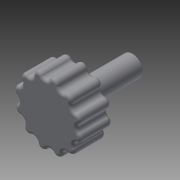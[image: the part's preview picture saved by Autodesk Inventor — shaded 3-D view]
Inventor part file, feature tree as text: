
AUTODESK INVENTOR PART (.ipt)
format: ipt  version: 2015 SP2 (Build 190223200, 223)  size: 412,672 bytes
history: native  units: mm
features: fillet x6, extrude x3, sketch x3, projected_geometry x1
ambient origin geometry x8: Origin, YZ Plane, XZ Plane, XY Plane, X Axis, Y Axis, Z Axis, Center Point
bodies: Body1 (feature_tree)
feature tree (13):
  extrude  "Extrusion2"  Depth=10.0mm
  fillet  "Rundung4"  [1 undecoded]
  fillet  "Rundung5"  Radius=120.0mm
  extrude  "Extrusion3"  Depth=1.0mm
  fillet  "Rundung6"  Radius=4.6mm
  fillet  "Rundung7"  Radius=6.5mm
  extrude  "Extrusion4"  Depth=0.2mm
  fillet  "Rundung8"  Radius=0.2mm
  fillet  "Rundung9"  Radius=3.0mm
  sketch  "Skizze3"  dims[d17=150.0mm d19=360.0deg d21=10.0mm d22=0.0mm d26=30.0mm d27=60.0deg d28=120.0mm d30=360.0deg]
  sketch  "Skizze5"  dims[d32=1.5mm d33=1.0mm d34=4.6mm d35=6.5mm]
  sketch  "Skizze6"  dims[d36=17.0mm d37=0.0mm d38=1.0mm d39=0.2mm d40=3.0mm d41=8.0mm d42=0.0mm d43=0.2mm d44=0.2mm]
  projected_geometry  "Projizierte Kontur1"
note: 1 required parameter value undecoded (feature->parameter linkage not recoverable at this tier; creation-order binding heuristic only, values carry confidence <= 0.55)
